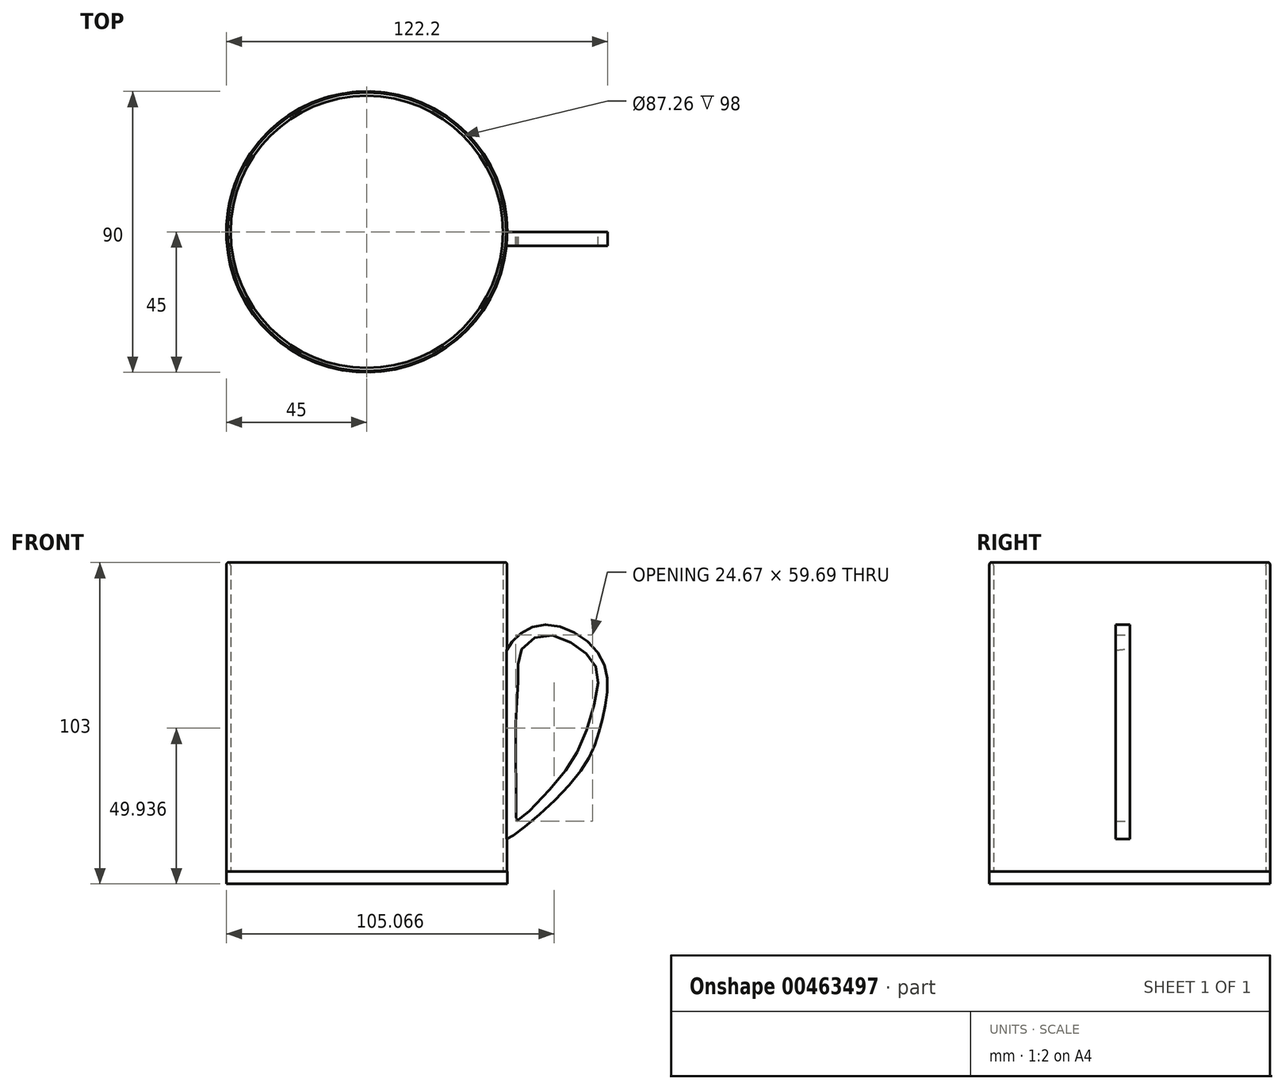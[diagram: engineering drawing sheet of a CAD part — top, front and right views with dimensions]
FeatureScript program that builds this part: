
annotation { "Feature Type Name" : "Feature", "Feature Type Description" : "" }
export const myFeature = defineFeature(function(context is Context, id is Id, definition is map)
    precondition{}
    {
        {
            var Q0;
            Q0=qCreatedBy(makeId("Top.planeOp"),FACE);
            var sketch = newSketch(context, id + "F0", { "sketchPlane" : qUnion([Q0])});
            skCircle(sketch, "E0", {"center": v(0, 0) * mm, "radius": 45 * mm});
            skSolve(sketch);
        }
        {
            var Q0;
            Q0 = qSketchRegion(id + "F0", true);
            extrude(context, id + "F1", {"entities" : qUnion([Q0]), "depth" : 4 * mm});
        }
        {
            var Q0;
            Q0=makeQuery(id+"F1.opExtrude","CAP_FACE",FACE,{"disambiguationData":[OSD([sQuery(id+"F0.wireOp",EDGE,"E0")])],"isStart":false});
            var sketch = newSketch(context, id + "F2", { "sketchPlane" : qUnion([Q0])});
            skCircle(sketch, "E1", {"center": v(0, 0) * mm, "radius": 44.98 * mm});
            skCircle(sketch, "E2", {"center": v(0, 0) * mm, "radius": 43.63 * mm});
            skSolve(sketch);
        }
        {
            var Q0;
            Q0=makeQuery(id+"F2.imprint","IMPRINT",FACE,{"disambiguationData":[TD([[makeQuery(id+"F2.imprint","IMPRINT",EDGE,{"derivedFrom":sQuery(id+"F2.wireOp",EDGE,"E1")}),1.0]])]});
            extrude(context, id + "F3", {"entities" : qUnion([Q0]), "operationType" : NewBodyOperationType.ADD, "depth" : 99 * mm});
        }
        {
            var Q0;
            Q0=makeQuery(id+"F3.opExtrude","CAP_EDGE",EDGE,{"disambiguationData":[OSD([sQuery(id+"F2.wireOp",EDGE,"E2")])],"isStart":false});
            fillet(context, id + "F4", {"entities" : qUnion([Q0]), "radius" : 1 * mm, "tangentPropagation" : true, "allowEdgeOverflow" : false});
        }
        {
            var Q0;
            Q0=makeQuery(id+"F3.opExtrude","CAP_EDGE",EDGE,{"disambiguationData":[OSD([sQuery(id+"F2.wireOp",EDGE,"E1")])],"isStart":false});
            fillet(context, id + "F5", {"entities" : qUnion([Q0]), "radius" : 1 * mm, "tangentPropagation" : true, "allowEdgeOverflow" : false});
        }
        {
            var Q0;
            Q0=qCreatedBy(makeId("Front.planeOp"),FACE);
            var sketch = newSketch(context, id + "F6", { "sketchPlane" : qUnion([Q0])});
            skFitSpline(sketch, "E3", {"points": [v(44.6, 74.5) * mm, v(56, 83.04) * mm, v(75.22, 72.36) * mm, v(75.57, 53.14) * mm, v(65.96, 32.85) * mm, v(44.6, 14.33) * mm, v(44.4, 15.08) * mm, v(44.27, 19.55) * mm, v(44.33, 31.7) * mm, v(44, 60.1) * mm, v(44, 69.1) * mm, v(44.6, 74.5) * mm]});
            skFitSpline(sketch, "E4", {"points": [v(48.04, 20.1) * mm, v(59.4, 31.15) * mm, v(68.23, 43.84) * mm, v(73.79, 61.72) * mm, v(73.03, 70.45) * mm, v(66.47, 76.71) * mm, v(56.33, 79.74) * mm, v(49.38, 74.64) * mm, v(48.57, 67.35) * mm, v(47.9, 55.21) * mm, v(47.73, 42.1) * mm, v(47.8, 31.92) * mm, v(47.89, 22.85) * mm, v(47.9, 21.21) * mm, v(48.04, 20.1) * mm]});
            skSolve(sketch);
        }
        {
            var Q0;
            Q0=makeQuery(id+"F6.imprint","IMPRINT",FACE,{"disambiguationData":[TD([[makeQuery(id+"F6.imprint","IMPRINT",EDGE,{"derivedFrom":sQuery(id+"F6.wireOp",EDGE,"E3")}),-1.0]])]});
            extrude(context, id + "F7", {"entities" : qUnion([Q0]), "operationType" : NewBodyOperationType.ADD, "depth" : 4.5 * mm});
        }
    });
